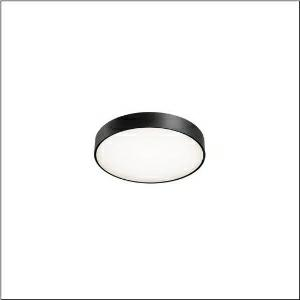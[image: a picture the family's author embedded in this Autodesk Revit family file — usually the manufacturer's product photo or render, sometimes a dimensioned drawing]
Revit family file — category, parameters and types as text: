
# Revit family: round_21_s_51mr34fd0321b
name_source: partatom
category: Lighting Fixtures
units: mm (PartAtom-declared; Revit-internal decimal feet)

## family parameters
Cut with Voids When Loaded = No
Host = Face
Light Source = No
Part Type = Normal
Room Calculation Point = No
Round Connector Dimension = Use Diameter
Shared = No

## types (1)
- Round 21 S (1 x LED, 3750 lm, 30.3 W, 3000K)
    Apparent Load = 30 VA
    CIE Flux Codes = 49 80 96 100 100
    Color Rendering = 80
    Color Temperature = 3000K
    Default Elevation = 1800 mm
    Description = Round 21 S, wall and ceiling luminaire, primary optical cover: cover, of PMMA, opal, light emission: direct distribution, primary light characteristic: symmetric, installation type: suspended mounting, surface-mounted, LED, rated luminous flux: 3.750lm, luminous efficacy: 124lm/W, light colour: 830, colour temperature: 3000K, control gear: DALI 2, with terminal, 5-pole, mains connection: 230V, AC, 50/60Hz, rated input power: 30.3W, housing, of aluminium, coated, black, diameter: 400mm, height: 62mm, protection rating (complete): IP40, insulation class (complete): insulation class I (protective earthing), certification: CE, impact resistance: IK04, permissible operating ambient temperature: -10..+35°C, packaging unit: 1 piece
    Height = 87 mm
    Lamp = 1 x LED
    Lamp Light Flux = 3750 lm
    Lamp Power = 30.3 W
    Lamp count = 1
    Length = 400 mm
    Luminous efficacy = 124 lm/W
    Manufacturer = Siteco
    ModVariant = No
    Model = 51MR34FD0321B
    Mounting Place = Ceiling
    Mounting Type = Surface mounted
    Number of Poles = 1
    OnlyDefault = Yes
    Power Factor = 1
    Product Name = Round 21 S
    Product group = wall and ceiling luminaire | ceiling mounted
    ProductGroupID = 304
    Protection Class = Protection class I
    Protection Degree = IP 40
    RLX_Detail_Level = 1
    RLX_Emergency_Light_Flux = 0 lm
    RLX_Emergency_Type = 0
    RLX_Emergency_Type_DB = No
    RlxData = <blob elided: 13465 chars, md5=29a01da9>
    Socket = socket
    Standby Power = 0 W
    System Light Flux = 3750 lm
    System Power = 30 W
    Type Comments = Product without accessories
    Type Image = l_1258311.jpg
    URL = http://relux.com
    VarID = ---
    Voltage = 0 V
    Weight = 0.00 kg
    Width = 0 mm  [stored 0 ft]

note: [stored X ft] marks values corroborated as IEEE doubles in the binary element streams (Revit-internal decimal feet)

## geometry (parser evidence)
native form markers: Sweep x10
no freeform markers — native parametric forms only
